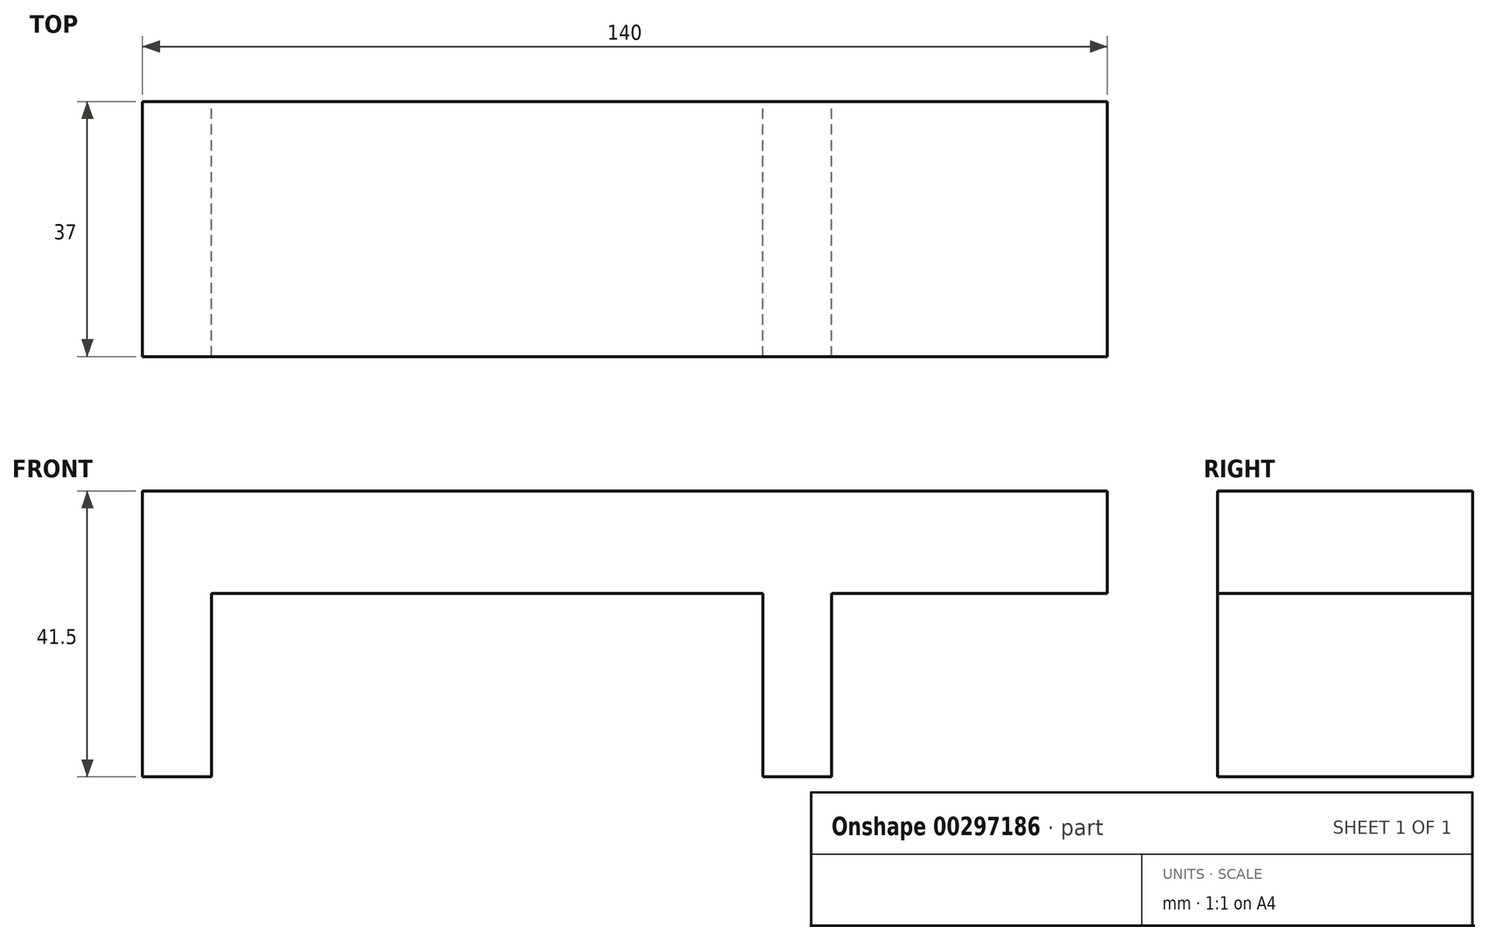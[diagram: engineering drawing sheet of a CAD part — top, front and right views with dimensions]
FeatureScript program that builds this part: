
annotation { "Feature Type Name" : "Feature", "Feature Type Description" : "" }
export const myFeature = defineFeature(function(context is Context, id is Id, definition is map)
    precondition{}
    {
        {
            var Q0;
            Q0=qCreatedBy(makeId("Top.planeOp"),FACE);
            var sketch = newSketch(context, id + "F0", { "sketchPlane" : qUnion([Q0])});
            skLineSegment(sketch, "E0.bottom", {"start": v(70, 18.5) * mm, "end": v(-70, 18.5) * mm});
            skLineSegment(sketch, "E0.top", {"start": v(70, -18.5) * mm, "end": v(-70, -18.5) * mm});
            skLineSegment(sketch, "E0.left", {"start": v(70, 18.5) * mm, "end": v(70, -18.5) * mm});
            skLineSegment(sketch, "E0.right", {"start": v(-70, 18.5) * mm, "end": v(-70, -18.5) * mm});
            skPoint(sketch, "E0.middle", {"position": v(0, 0) * mm});
            skLineSegment(sketch, "E1.bottom", {"start": v(0, 18.5) * mm, "end": v(70, 18.5) * mm});
            skLineSegment(sketch, "E1.top", {"start": v(0, -18.5) * mm, "end": v(70, -18.5) * mm});
            skLineSegment(sketch, "E1.left", {"start": v(0, 18.5) * mm, "end": v(0, -18.5) * mm});
            skSolve(sketch);
        }
        {
            var Q0;
            Q0=makeQuery(id+"F0.imprint","IMPRINT",FACE,{"disambiguationData":[TD([[makeQuery(id+"F0.imprint","IMPRINT",EDGE,{"derivedFrom":sQuery(id+"F0.wireOp",EDGE,"E0.bottom")}),1.0]])]});
            extrude(context, id + "F1", {"entities" : qUnion([Q0]), "depth" : 41.5 * mm});
        }
        {
            var Q0;
            Q0 = qSketchRegion(id + "F0", true);
            extrude(context, id + "F2", {"entities" : qUnion([Q0]), "operationType" : NewBodyOperationType.ADD, "depth" : 35.5 * mm});
        }
        {
            var Q0;
            {var subQ0=sQuery(id+"F0.wireOp",EDGE,"E0.bottom");Q0=makeQuery(id+"F2.boolean.opBoolean","MERGE",FACE,{"derivedFrom":[makeQuery(id+"F1.opExtrude","SWEPT_FACE",FACE,{"disambiguationData":[OSD([subQ0])]}),makeQuery(id+"F2.opExtrude","SWEPT_FACE",FACE,{"disambiguationData":[OSD([subQ0,sQuery(id+"F0.wireOp",EDGE,"E1.bottom")])]})]});}
            var sketch = newSketch(context, id + "F3", { "sketchPlane" : qUnion([Q0])});
            skLineSegment(sketch, "E2.bottom", {"start": v(-70, 0) * mm, "end": v(-30, 0) * mm});
            skLineSegment(sketch, "E2.top", {"start": v(-70, 26.64) * mm, "end": v(-30, 26.64) * mm});
            skLineSegment(sketch, "E2.left", {"start": v(-70, 0) * mm, "end": v(-70, 26.64) * mm});
            skLineSegment(sketch, "E2.right", {"start": v(-30, 0) * mm, "end": v(-30, 26.64) * mm});
            skLineSegment(sketch, "E3.bottom", {"start": v(-20, 0) * mm, "end": v(60, 0) * mm});
            skLineSegment(sketch, "E3.top", {"start": v(-20, 26.64) * mm, "end": v(60, 26.64) * mm});
            skLineSegment(sketch, "E3.left", {"start": v(-20, 0) * mm, "end": v(-20, 26.64) * mm});
            skLineSegment(sketch, "E3.right", {"start": v(60, 0) * mm, "end": v(60, 26.64) * mm});
            skSolve(sketch);
        }
        {
            var Q0;
            Q0=makeQuery(id+"F3.imprint","IMPRINT",FACE,{"disambiguationData":[TD([[makeQuery(id+"F3.imprint","IMPRINT",EDGE,{"derivedFrom":sQuery(id+"F3.wireOp",EDGE,"E3.bottom")}),1.0]])]});
            var Q1;
            Q1=makeQuery(id+"F3.imprint","IMPRINT",FACE,{"disambiguationData":[TD([[makeQuery(id+"F3.imprint","IMPRINT",EDGE,{"derivedFrom":sQuery(id+"F3.wireOp",EDGE,"E2.bottom")}),1.0]])]});
            extrude(context, id + "F4", {"entities" : qUnion([Q0, Q1]), "operationType" : NewBodyOperationType.REMOVE, "oppositeDirection" : true, "depth" : 40 * mm});
        }
    });
